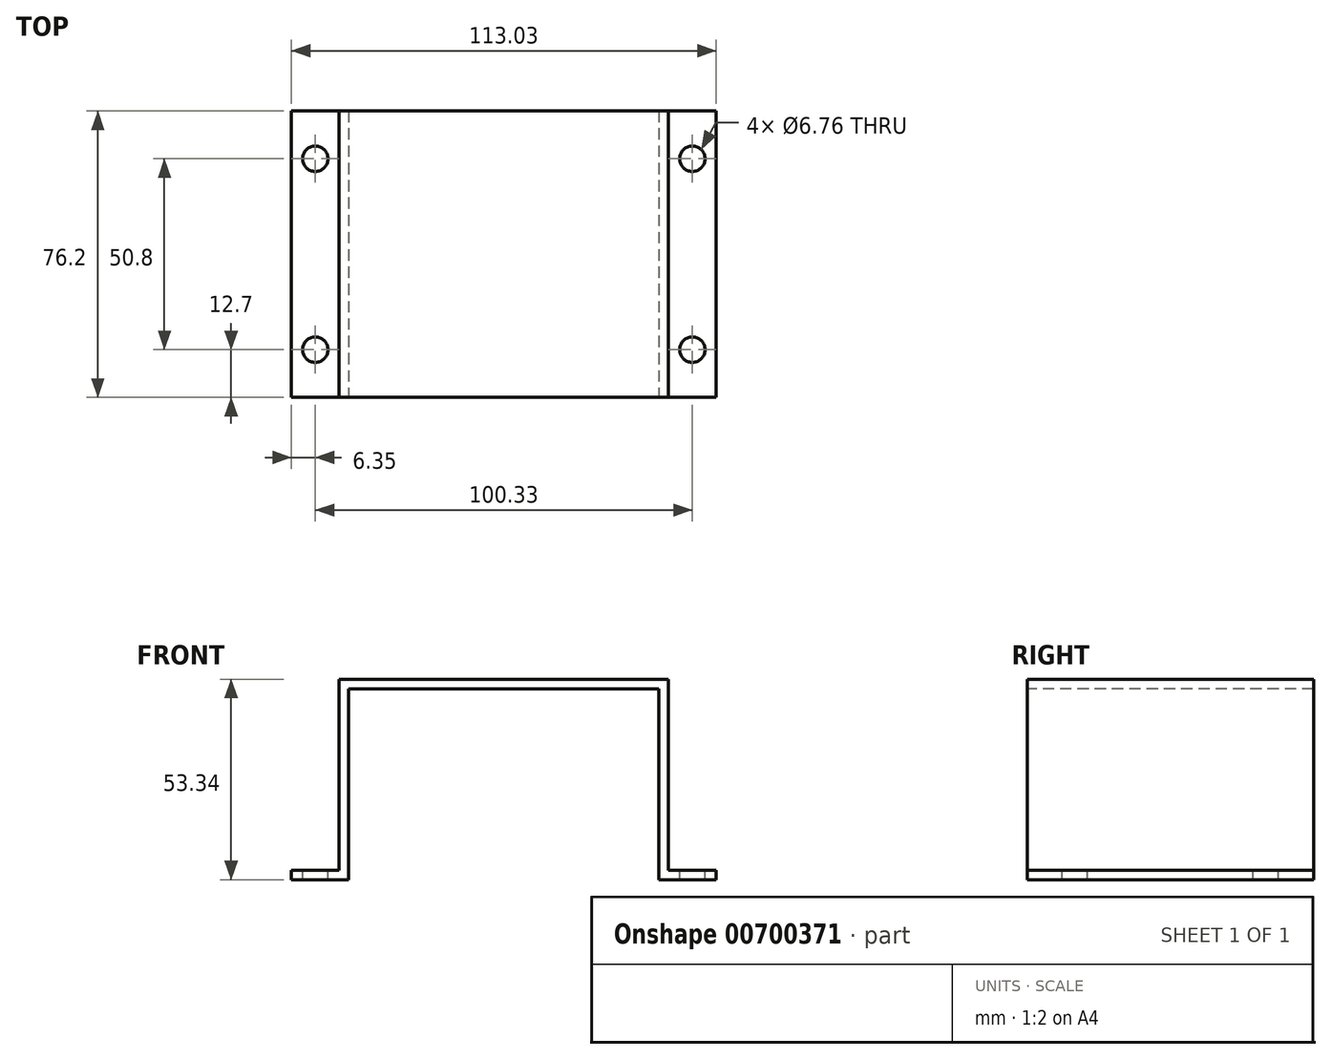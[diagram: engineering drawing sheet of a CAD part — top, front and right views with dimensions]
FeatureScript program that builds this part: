
annotation { "Feature Type Name" : "Feature", "Feature Type Description" : "" }
export const myFeature = defineFeature(function(context is Context, id is Id, definition is map)
    precondition{}
    {
        {
            var Q0;
            Q0=qCreatedBy(makeId("Front.planeOp"),FACE);
            var sketch = newSketch(context, id + "F0", { "sketchPlane" : qUnion([Q0])});
            skLineSegment(sketch, "E0", {"start": v(0, 0) * mm, "end": v(0, 2.54) * mm});
            skLineSegment(sketch, "E1", {"start": v(0, 2.54) * mm, "end": v(12.7, 2.54) * mm});
            skLineSegment(sketch, "E2", {"start": v(12.7, 2.54) * mm, "end": v(12.7, 53.34) * mm});
            skLineSegment(sketch, "E3", {"start": v(12.7, 53.34) * mm, "end": v(100.33, 53.34) * mm});
            skLineSegment(sketch, "E4", {"start": v(97.8, 50.8) * mm, "end": v(15.24, 50.8) * mm});
            skLineSegment(sketch, "E5", {"start": v(15.24, 50.8) * mm, "end": v(15.24, 0) * mm});
            skLineSegment(sketch, "E6", {"start": v(15.24, 0) * mm, "end": v(0, 0) * mm});
            skLineSegment(sketch, "E7", {"start": v(97.8, 50.8) * mm, "end": v(97.8, 0) * mm});
            skLineSegment(sketch, "E8", {"start": v(97.8, 0) * mm, "end": v(113.03, 0) * mm});
            skLineSegment(sketch, "E9", {"start": v(113.03, 0) * mm, "end": v(113.03, 2.54) * mm});
            skLineSegment(sketch, "E10", {"start": v(113.03, 2.54) * mm, "end": v(100.33, 2.54) * mm});
            skLineSegment(sketch, "E11", {"start": v(100.33, 2.54) * mm, "end": v(100.33, 53.34) * mm});
            skSolve(sketch);
        }
        {
            var Q0;
            Q0 = qSketchRegion(id + "F0", true);
            extrude(context, id + "F1", {"entities" : qUnion([Q0]), "oppositeDirection" : true, "depth" : 76.2 * mm, "offsetDistance" : 25.4 * mm});
        }
        {
            var Q0;
            Q0=makeQuery(id+"F1.opExtrude","SWEPT_FACE",FACE,{"disambiguationData":[OSD([sQuery(id+"F0.wireOp",EDGE,"E1")])]});
            var sketch = newSketch(context, id + "F2", { "sketchPlane" : qUnion([Q0])});
            skPoint(sketch, "E12", {"position": v(6.35, 63.5) * mm});
            skPoint(sketch, "E13", {"position": v(6.35, 12.7) * mm});
            skPoint(sketch, "E14", {"position": v(106.68, 63.5) * mm});
            skPoint(sketch, "E15", {"position": v(106.68, 12.7) * mm});
            skLineSegment(sketch, "E16", {"start": v(6.35, 76.2) * mm, "end": v(6.35, 0) * mm, "construction": true});
            skLineSegment(sketch, "E17", {"start": v(106.68, 0) * mm, "end": v(106.68, 76.2) * mm, "construction": true});
            skSolve(sketch);
        }
        {
            var Q0;
            Q0=sQuery(id+"F2.wireOp",VERTEX,"E12");
            var Q1;
            Q1=sQuery(id+"F2.wireOp",VERTEX,"E13");
            var Q2;
            Q2=sQuery(id+"F2.wireOp",VERTEX,"E15");
            var Q3;
            Q3=sQuery(id+"F2.wireOp",VERTEX,"E14");
            var Q4;
            Q4=makeQuery(id+"F1.opExtrude","SWEPT_BODY",BODY,{"disambiguationData":[OSD([sQuery(id+"F0.wireOp",EDGE,"E0"),sQuery(id+"F0.wireOp",EDGE,"E1"),sQuery(id+"F0.wireOp",EDGE,"E2"),sQuery(id+"F0.wireOp",EDGE,"E3"),sQuery(id+"F0.wireOp",EDGE,"E4"),sQuery(id+"F0.wireOp",EDGE,"E5"),sQuery(id+"F0.wireOp",EDGE,"E6"),sQuery(id+"F0.wireOp",EDGE,"E7"),sQuery(id+"F0.wireOp",EDGE,"E8"),sQuery(id+"F0.wireOp",EDGE,"E9"),sQuery(id+"F0.wireOp",EDGE,"E10"),sQuery(id+"F0.wireOp",EDGE,"E11")])]});
            hole(context, id + "F3", {"style" : HoleStyle.SIMPLE, "endStyle" : HoleEndStyle.THROUGH, "standardTappedOrClearance" : lookupTablePath({ "standard" : "ANSI", "fit" : "Normal (ASME)", "size" : "1/4", "type" : "Clearance" }), "standardBlindInLast" : lookupTablePath({ "fit" : "Free", "standard" : "ANSI", "size" : "1/4", "type" : "Clearance" }), "holeDiameter" : 6.76 * mm, "majorDiameter" : 6.35 * mm, "isTappedThrough" : true, "tappedDepth" : 10.32 * mm, "tapClearance" : 3, "startFromSketch" : true, "locations" : qUnion([Q0, Q1, Q2, Q3]), "scope" : qUnion([Q4])});
        }
    });
